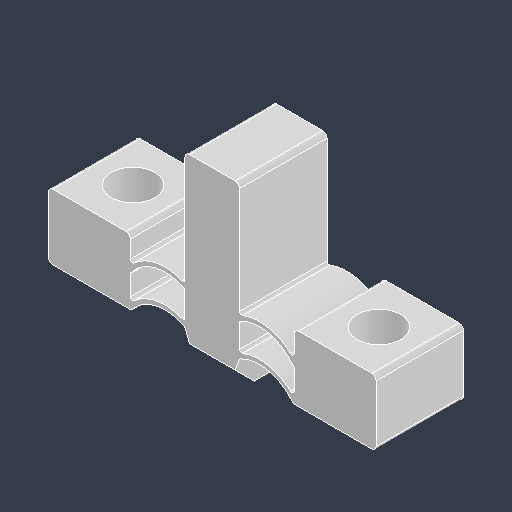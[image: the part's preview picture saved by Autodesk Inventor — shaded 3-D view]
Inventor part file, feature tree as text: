
AUTODESK INVENTOR PART (.ipt)
format: ipt  version: 2023.4 (Build 274418000, 418)  size: 220,160 bytes
history: native  units: mm
features: chamfer x2, fillet x2, sketch x2, extrude x1, hole x1
ambient origin geometry x8: Origin, YZ Plane, XZ Plane, XY Plane, X Axis, Y Axis, Z Axis, Center Point
bodies: Solid1 (feature_tree)
feature tree (8):
  extrude  "Extrusion1"  Depth=18.0mm
  chamfer  "Chamfer1"  Distance=3.0mm
  chamfer  "Chamfer2"  Distance=3.0mm
  fillet  "Fillet1"  Radius=5.0mm
  fillet  "Fillet2"  Radius=9.0mm
  hole  "Hole2"  [1 undecoded]
  sketch  "Sketch1"  dims[d0=5.0mm d1=18.0mm]
  sketch  "Sketch3"  dims[d2=30.0mm d3=3.0mm d4=3.0mm d5=5.0mm d8=9.0mm d9=3.0mm d10=2.0mm d11=3.490659mm d12=0.4mm d13=4.0mm d14=3.0mm d15=8.0mm d16=0.0mm d25=3.0mm d26=2.0mm d27=45.0deg d28=3.0mm d29=2.0mm d30=45.0deg d31=0.2mm d32=0.4mm d34=4.0mm d35=6.0mm d36=4.0mm d37=2.0mm d38=90.0deg d39=8.0mm d40=20.594885mm]
note: 1 required parameter value undecoded (feature->parameter linkage not recoverable at this tier; creation-order binding heuristic only, values carry confidence <= 0.55)
